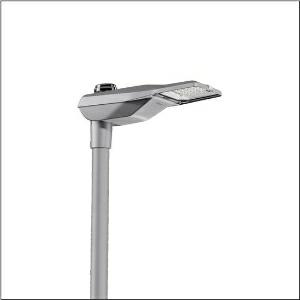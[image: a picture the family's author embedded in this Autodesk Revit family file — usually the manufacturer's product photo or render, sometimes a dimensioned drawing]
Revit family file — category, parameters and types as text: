
# Revit family: streetlight_sl_21_micro___pl52_5xe5h37n08cb_9265
name_source: partatom
category: Lighting Fixtures
units: mm (PartAtom-declared; Revit-internal decimal feet)

## family parameters
Cut with Voids When Loaded = No
Host = Face
Light Source = No
Part Type = Normal
Room Calculation Point = No
Round Connector Dimension = Use Diameter
Shared = No

## types (1)
- --- (1 x LED, 2250 lm, 15.8 W, 3000K)
    Apparent Load = 16 VA
    CIE Flux Codes = 27 59 98 100 100
    Color Rendering = 70
    Color Temperature = 3000K
    Default Elevation = 1800 mm
    Description = Streetlight SL 21 micro, mast luminaire, primary light control with lens, of PMMA, primary optical cover: cover, of toughened safety glass, transparent, light distribution: PL52, light emission: direct distribution, primary light characteristic: asymmetric, installation type: post-top, LED, 3G 1.5mm², High Power LED, rated luminous flux: 2.250lm, luminous efficacy: 142lm/W, light colour: 730, colour temperature: 3000K, control gear: NEMA (7pin), control: overheat protection, pre-setting: linear dimming characteristic, constant luminous flux control, time-dependent luminous flux control, flexible luminous flux parameterisation, mains connection: 230..240V, AC, 50/60Hz, connection cable pre-assembled, cable length: 6,5m, wiring characteristics: H07RN-F, start of lifetime: 16W, end of service life: 16W, reduction: 8W, luminaire housing, of diecast aluminium (EN AC-44300), powder-coated, SITECO metallic grey (DB 702S), corrosivity category C5 high according to DIN EN ISO 12944, multi-level sealing system, sealing non-destructively replaceable, inclination adjustable: 0°, 5°, 10°, 15°, length: 528mm, width: 235mm, height: 110mm, spigot size: 76/60mm (post-top), mounting height: 4..8m, protection rating (complete): IP66, insulation class (complete): insulation class I (protective earthing), certification: CE, ENEC, ENEC+, VDE, impact resistance: IK10, permissible operating ambient temperature for outdoor applications: -40..+50°C, standard-compliant lighting for roads and squares, packaging unit: 1 piece

Light Distribution: PL52
    Height = 110 mm
    Lamp = 1 x LED
    Lamp Light Flux = 2250 lm
    Lamp Power = 15.8 W
    Lamp count = 1
    Length = 528 mm
    Luminous efficacy = 142 lm/W
    Manufacturer = Siteco
    ModVariant = No
    Model = 5XE5H37N08CB
    Number of Poles = 1
    OnlyDefault = Yes
    Power Factor = 1
    Product Name = Streetlight SL 21 micro | PL52
    Product group = mast luminaire | pylon top
    ProductGroupID = 6100
    Protection Class = Protection class I
    Protection Degree = IP 66
    RLX_Detail_Level = 1
    RLX_Emergency_Light_Flux = 0 lm
    RLX_Emergency_Type = 0
    RLX_Emergency_Type_DB = No
    RlxData = <blob elided: 108085 chars, md5=0b0034c5>
    Socket = socket
    Standby Power = 0 W
    System Light Flux = 2250 lm
    System Power = 16 W
    Type Comments = factory setting: luminous flux: 100 % | dim-lin: 254 | 300 mA
    Type Image = l_1294375.jpg
    URL = http://relux.com
    VarID = @adj_136725
    Voltage = 0 V
    Weight = 0.00 kg
    Width = 235 mm

## geometry (parser evidence)
native form markers: Blend x4, Sweep x10
no freeform markers — native parametric forms only
